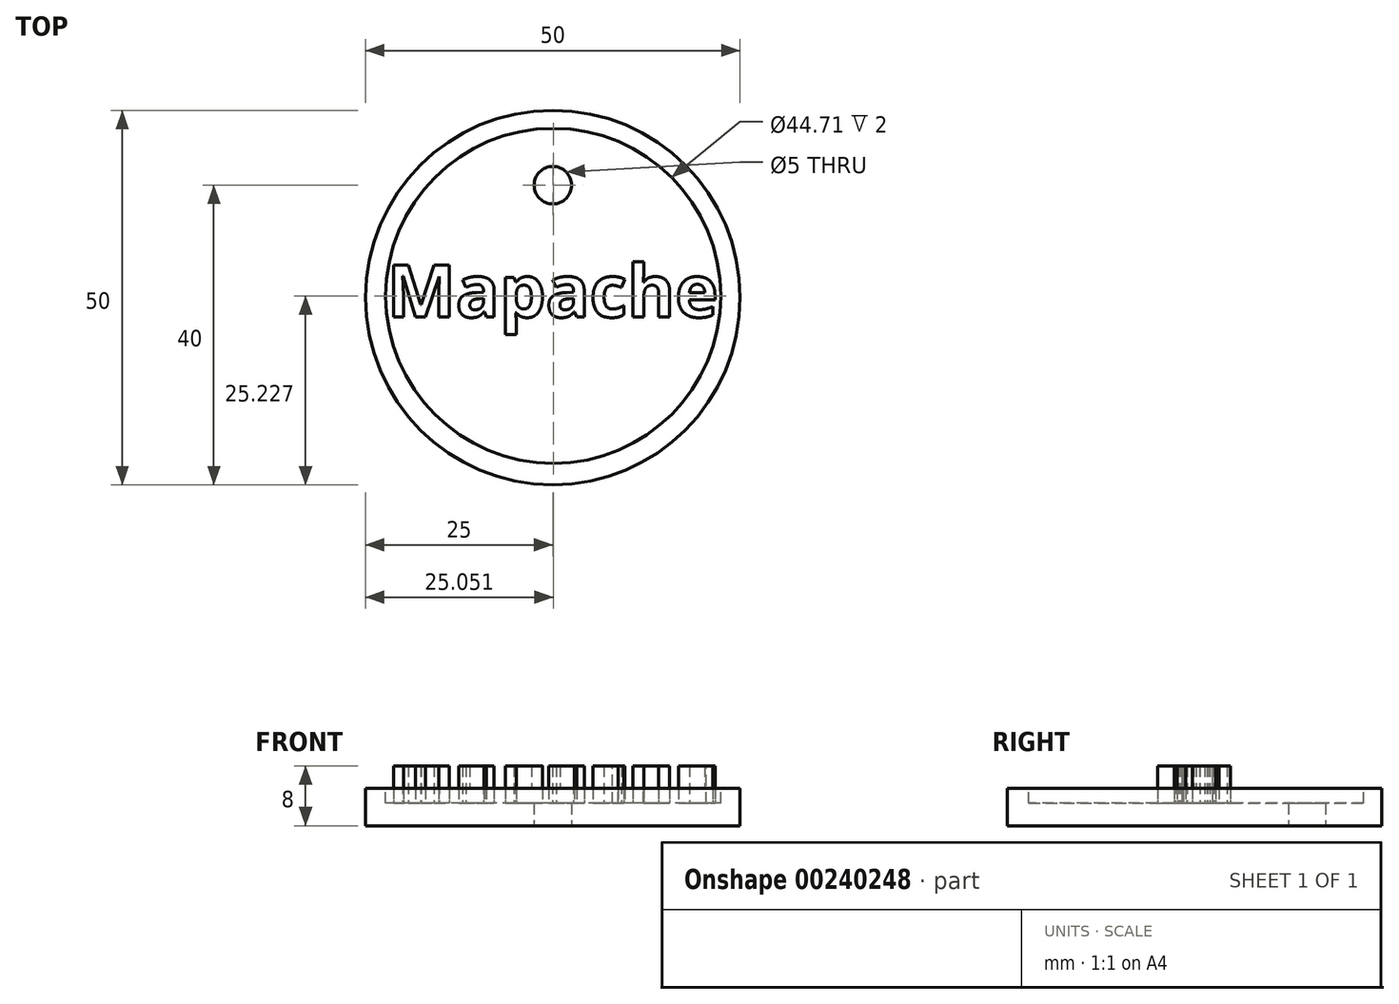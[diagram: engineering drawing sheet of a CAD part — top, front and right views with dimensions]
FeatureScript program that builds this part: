
annotation { "Feature Type Name" : "Feature", "Feature Type Description" : "" }
export const myFeature = defineFeature(function(context is Context, id is Id, definition is map)
    precondition{}
    {
        {
            var Q0;
            Q0=qCreatedBy(makeId("Top.planeOp"),FACE);
            var sketch = newSketch(context, id + "F0", { "sketchPlane" : qUnion([Q0])});
            skCircle(sketch, "E0", {"center": v(0, 0) * mm, "radius": 25 * mm});
            skLineSegment(sketch, "E1", {"start": v(0, 0) * mm, "end": v(0, 15) * mm, "construction": true});
            skCircle(sketch, "E2", {"center": v(0, 15) * mm, "radius": 2.5 * mm});
            skSolve(sketch);
        }
        {
            var Q0;
            Q0 = qSketchRegion(id + "F0", true);
            extrude(context, id + "F1", {"entities" : qUnion([Q0]), "depth" : 5 * mm});
        }
        {
            var Q0;
            Q0=makeQuery(id+"F1.opExtrude","CAP_FACE",FACE,{"disambiguationData":[OSD([sQuery(id+"F0.wireOp",EDGE,"E0"),sQuery(id+"F0.wireOp",EDGE,"E2")])],"isStart":false});
            var sketch = newSketch(context, id + "F2", { "sketchPlane" : qUnion([Q0])});
            skText(sketch, "E3", { "text": "Mapache", "fontName": "OpenSans-Bold.ttf"});
            const initialGuessF2  = {"E3": [-0.02214, -0.0026, 1, 0, 0.007]};
            skSetInitialGuess(sketch, initialGuessF2);
            skSolve(sketch);
        }
        {
            var Q0;
            Q0 = qSketchRegion(id + "F2", true);
            extrude(context, id + "F3", {"entities" : qUnion([Q0]), "operationType" : NewBodyOperationType.ADD, "depth" : 3 * mm});
        }
        {
            var Q0;
            {var subQ0=sQuery(id+"F0.wireOp",EDGE,"E2");var subQ1=sQuery(id+"F0.wireOp",EDGE,"E0");Q0=makeQuery(id+"F3.boolean.opBoolean","SPLIT",FACE,{"disambiguationData":[TD([makeQuery(id+"F1.opExtrude","SWEPT_FACE",FACE,{"disambiguationData":[OSD([subQ1])]})])],"derivedFrom":makeQuery(id+"F1.opExtrude","CAP_FACE",FACE,{"disambiguationData":[OSD([subQ1,subQ0])],"isStart":false})});}
            var sketch = newSketch(context, id + "F4", { "sketchPlane" : qUnion([Q0])});
            skCircle(sketch, "E4", {"center": v(0.05, 0.23) * mm, "radius": 22.36 * mm});
            skSolve(sketch);
        }
        {
            var Q0;
            Q0=makeQuery(id+"F4.imprint","IMPRINT",FACE,{"disambiguationData":[TD([[makeQuery(id+"F4.imprint","IMPRINT",EDGE,{"derivedFrom":sQuery(id+"F4.wireOp",EDGE,"E4")}),1.0]])]});
            var Q1;
            Q1=sQuery(id+"F4.wireOp",EDGE,"E4");
            extrude(context, id + "F5", {"entities" : qUnion([Q0]), "operationType" : NewBodyOperationType.REMOVE, "surfaceEntities" : qUnion([Q1]), "oppositeDirection" : true, "depth" : 2 * mm});
        }
    });
